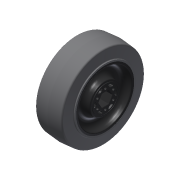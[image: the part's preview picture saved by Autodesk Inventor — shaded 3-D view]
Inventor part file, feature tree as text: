
AUTODESK INVENTOR PART (.ipt)
format: ipt  version: 2015 (Build 190159000, 159)  size: 3,585,024 bytes
history: native  units: in
note: dims shown in document units (in); Inventor stores cm internally (conversion verified against a paired STEP export)
features: other x2, extrude x1, mirror x1, imported_body x1, sketch x1
ambient origin geometry x8: Origin, YZ Plane, XZ Plane, XY Plane, X Axis, Y Axis, Z Axis, Center Point
bodies: Body1 (feature_tree)
feature tree (6):
  parser-record x1  (decoder bookkeeping rows leaked as tree rows — omitted from the tree; the rows remain in map.json)
  other  "217-4048-STEP-201410301"
  extrude  "Extrusion1"  Depth=2.2441in
  mirror  "Mirror1"
  imported_body  "Base1"
  sketch  "Sketch1"  dims[d0=2.3819in d2=2.2441in d3=0.0039in d4=0.0in]
